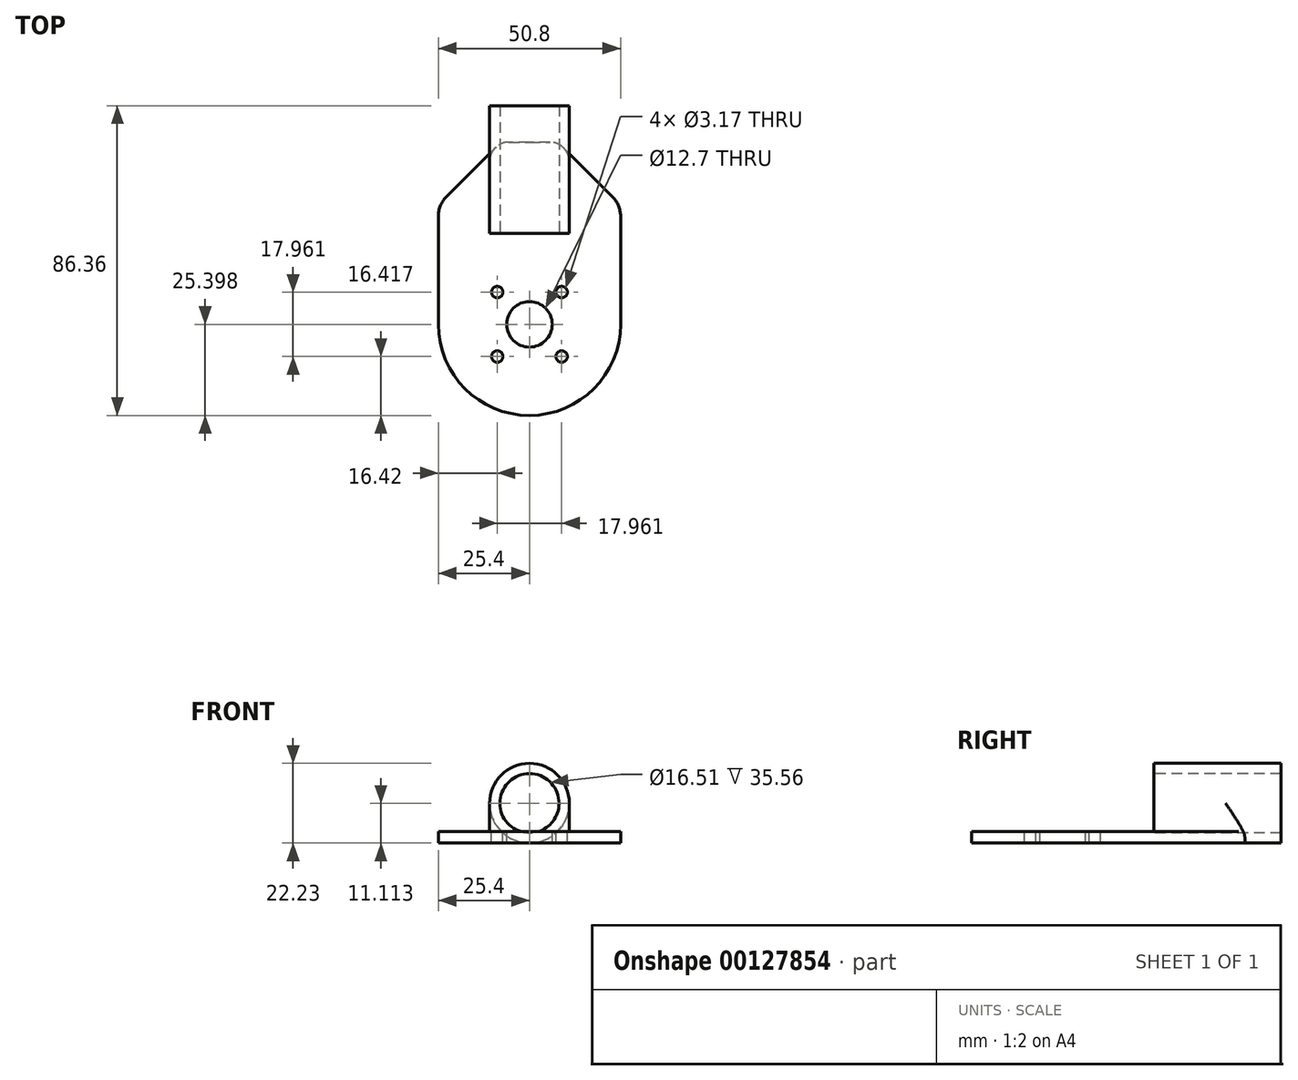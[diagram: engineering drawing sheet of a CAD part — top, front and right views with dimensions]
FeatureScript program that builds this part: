
annotation { "Feature Type Name" : "Feature", "Feature Type Description" : "" }
export const myFeature = defineFeature(function(context is Context, id is Id, definition is map)
    precondition{}
    {
        {
            var Q0;
            Q0=qCreatedBy(makeId("Top.planeOp"),FACE);
            var sketch = newSketch(context, id + "F0", { "sketchPlane" : qUnion([Q0])});
            skCircle(sketch, "E0", {"center": v(0, 0) * mm, "radius": 11.11 * mm});
            skSolve(sketch);
        }
        {
            var Q0;
            Q0 = qSketchRegion(id + "F0", true);
            extrude(context, id + "F1", {"entities" : qUnion([Q0]), "depth" : 10.16 * mm, "hasSecondDirection" : true, "secondDirectionOppositeDirection" : true, "secondDirectionDepth" : 25.4 * mm});
        }
        {
            var Q0;
            Q0=makeQuery(id+"F1.opExtrude","CAP_FACE",FACE,{"disambiguationData":[OSD([sQuery(id+"F0.wireOp",EDGE,"E0")])],"isStart":false});
            var sketch = newSketch(context, id + "F2", { "sketchPlane" : qUnion([Q0])});
            skLineSegment(sketch, "E1.bottom", {"start": v(25.4, -11.11) * mm, "end": v(-25.4, -11.11) * mm});
            skLineSegment(sketch, "E1.top", {"start": v(25.4, -7.94) * mm, "end": v(-25.4, -7.94) * mm});
            skLineSegment(sketch, "E1.left", {"start": v(25.4, -11.11) * mm, "end": v(25.4, -7.94) * mm});
            skLineSegment(sketch, "E1.right", {"start": v(-25.4, -11.11) * mm, "end": v(-25.4, -7.94) * mm});
            skPoint(sketch, "E1.middle", {"position": v(0, -9.53) * mm});
            skSolve(sketch);
        }
        {
            var Q0;
            Q0 = qSketchRegion(id + "F2", true);
            extrude(context, id + "F3", {"entities" : qUnion([Q0]), "operationType" : NewBodyOperationType.ADD, "depth" : 50.8 * mm, "hasSecondDirection" : true, "secondDirectionOppositeDirection" : true, "secondDirectionDepth" : 25.4 * mm});
        }
        {
            var Q0;
            Q0=makeQuery(id+"F3.opExtrude","SWEPT_FACE",FACE,{"disambiguationData":[OSD([sQuery(id+"F2.wireOp",EDGE,"E1.top")])]});
            var sketch = newSketch(context, id + "F4", { "sketchPlane" : qUnion([Q0])});
            skPoint(sketch, "E2", {"position": v(0, 35.56) * mm});
            skCircle(sketch, "E3", {"center": v(-8.98, 26.58) * mm, "radius": 1.59 * mm});
            skCircle(sketch, "E4", {"center": v(-8.98, 44.54) * mm, "radius": 1.59 * mm});
            skCircle(sketch, "E5", {"center": v(8.98, 26.58) * mm, "radius": 1.59 * mm});
            skCircle(sketch, "E6", {"center": v(8.98, 44.54) * mm, "radius": 1.59 * mm});
            skSolve(sketch);
        }
        {
            var Q0;
            Q0 = qSketchRegion(id + "F4", true);
            extrude(context, id + "F5", {"entities" : qUnion([Q0]), "operationType" : NewBodyOperationType.REMOVE, "oppositeDirection" : true, "depth" : 25.4 * mm});
        }
        {
            var Q0;
            Q0=makeQuery(id+"F3.opExtrude","SWEPT_FACE",FACE,{"disambiguationData":[OSD([sQuery(id+"F2.wireOp",EDGE,"E1.bottom")])]});
            var sketch = newSketch(context, id + "F6", { "sketchPlane" : qUnion([Q0])});
            skArc(sketch, "E7", {"start": v(25.4, 35.56) * mm, "mid": v(0, 60.96) * mm, "end": v(-25.4, 35.56) * mm});
            skLineSegment(sketch, "E8", {"start": v(-25.4, 35.56) * mm, "end": v(-25.4, 60.96) * mm});
            skLineSegment(sketch, "E9", {"start": v(-25.4, 60.96) * mm, "end": v(25.4, 60.96) * mm});
            skLineSegment(sketch, "E10", {"start": v(25.4, 60.96) * mm, "end": v(25.4, 35.56) * mm});
            skSolve(sketch);
        }
        {
            var Q0;
            Q0 = qSketchRegion(id + "F6", true);
            extrude(context, id + "F7", {"entities" : qUnion([Q0]), "operationType" : NewBodyOperationType.REMOVE, "oppositeDirection" : true, "depth" : 25.4 * mm});
        }
        {
            var Q0;
            Q0=qCreatedBy(makeId("Top.planeOp"),FACE);
            cPlane(context, id + "F8", {"entities" : qUnion([Q0]), "cplaneType" : CPlaneType.OFFSET, "offset" : 10.16 * mm, "width" : 152.4 * mm, "height" : 152.4 * mm});
        }
        {
            var Q0;
            Q0=qCreatedBy(id+"F8.planeOp",FACE);
            var sketch = newSketch(context, id + "F9", { "sketchPlane" : qUnion([Q0])});
            skArc(sketch, "E11", {"start": v(11.11, 0) * mm, "mid": v(0, 11.11) * mm, "end": v(-11.11, 0) * mm});
            skLineSegment(sketch, "E12", {"start": v(-11.11, 0) * mm, "end": v(-11.11, -8.9) * mm});
            skLineSegment(sketch, "E13", {"start": v(11.11, 0) * mm, "end": v(11.11, -8.9) * mm});
            skLineSegment(sketch, "E14", {"start": v(-11.11, -8.9) * mm, "end": v(11.11, -8.9) * mm});
            skSolve(sketch);
        }
        {
            var Q0;
            Q0 = qSketchRegion(id + "F9", true);
            extrude(context, id + "F10", {"entities" : qUnion([Q0]), "operationType" : NewBodyOperationType.ADD, "oppositeDirection" : true, "depth" : 25.4 * mm});
        }
        {
            var Q0;
            Q0=makeQuery(id+"F3.opExtrude","CAP_EDGE",EDGE,{"disambiguationData":[OSD([sQuery(id+"F2.wireOp",EDGE,"E1.left")])],"isStart":true});
            var Q1;
            Q1=makeQuery(id+"F3.opExtrude","CAP_EDGE",EDGE,{"disambiguationData":[OSD([sQuery(id+"F2.wireOp",EDGE,"E1.right")])],"isStart":true});
            chamfer(context, id + "F11", {"entities" : qUnion([Q0, Q1]), "width" : 17.53 * mm, "tangentPropagation" : true});
        }
        {
            var Q0;
            {var subQ0=sQuery(id+"F2.wireOp",EDGE,"E1.left");Q0=makeQuery(id+"F11.opChamfer","BLEND_EDGE",EDGE,{"blendedFrom":[makeQuery(id+"F3.opExtrude","CAP_EDGE",EDGE,{"disambiguationData":[OSD([subQ0])],"isStart":true}),makeQuery(id+"F3.opExtrude","SWEPT_FACE",FACE,{"disambiguationData":[OSD([subQ0])]})],"blendedInto":[makeQuery(id+"F3.opExtrude","SWEPT_FACE",FACE,{"disambiguationData":[OSD([subQ0])]})]});}
            var Q1;
            {var subQ0=sQuery(id+"F2.wireOp",EDGE,"E1.right");Q1=makeQuery(id+"F11.opChamfer","BLEND_EDGE",EDGE,{"blendedFrom":[makeQuery(id+"F3.opExtrude","CAP_EDGE",EDGE,{"disambiguationData":[OSD([subQ0])],"isStart":true}),makeQuery(id+"F3.opExtrude","SWEPT_FACE",FACE,{"disambiguationData":[OSD([subQ0])]})],"blendedInto":[makeQuery(id+"F3.opExtrude","SWEPT_FACE",FACE,{"disambiguationData":[OSD([subQ0])]})]});}
            fillet(context, id + "F12", {"entities" : qUnion([Q0, Q1]), "radius" : 7.62 * mm, "tangentPropagation" : true, "allowEdgeOverflow" : false});
        }
        {
            var Q0;
            {var subQ0=sQuery(id+"F2.wireOp",EDGE,"E1.top");var subQ1=sQuery(id+"F2.wireOp",EDGE,"E1.left");var subQ2=sQuery(id+"F2.wireOp",EDGE,"E1.bottom");var subQ3=makeQuery(id+"F3.opExtrude","CAP_FACE",FACE,{"disambiguationData":[OSD([subQ2,subQ0,subQ1,sQuery(id+"F2.wireOp",EDGE,"E1.right")])],"isStart":true});Q0=makeQuery(id+"F11.opChamfer","BLEND_EDGE",EDGE,{"blendedFrom":[makeQuery(id+"F3.opExtrude","CAP_EDGE",EDGE,{"disambiguationData":[OSD([subQ1])],"isStart":true}),makeQuery(id+"F3.boolean.opBoolean","SPLIT",FACE,{"disambiguationData":[TD([makeQuery(id+"F3.opExtrude","SWEPT_FACE",FACE,{"disambiguationData":[OSD([subQ1])]})])],"derivedFrom":subQ3})],"blendedInto":[makeQuery(id+"F3.boolean.opBoolean","SPLIT",FACE,{"disambiguationData":[TD([makeQuery(id+"F3.opExtrude","SWEPT_FACE",FACE,{"disambiguationData":[OSD([subQ1])]})])],"derivedFrom":subQ3})]});}
            var Q1;
            {var subQ0=sQuery(id+"F2.wireOp",EDGE,"E1.top");var subQ1=sQuery(id+"F2.wireOp",EDGE,"E1.right");var subQ2=sQuery(id+"F2.wireOp",EDGE,"E1.bottom");var subQ3=makeQuery(id+"F3.opExtrude","CAP_FACE",FACE,{"disambiguationData":[OSD([subQ2,subQ0,sQuery(id+"F2.wireOp",EDGE,"E1.left"),subQ1])],"isStart":true});Q1=makeQuery(id+"F11.opChamfer","BLEND_EDGE",EDGE,{"blendedFrom":[makeQuery(id+"F3.opExtrude","CAP_EDGE",EDGE,{"disambiguationData":[OSD([subQ1])],"isStart":true}),makeQuery(id+"F3.boolean.opBoolean","SPLIT",FACE,{"disambiguationData":[TD([makeQuery(id+"F3.opExtrude","SWEPT_FACE",FACE,{"disambiguationData":[OSD([subQ1])]})])],"derivedFrom":subQ3})],"blendedInto":[makeQuery(id+"F3.boolean.opBoolean","SPLIT",FACE,{"disambiguationData":[TD([makeQuery(id+"F3.opExtrude","SWEPT_FACE",FACE,{"disambiguationData":[OSD([subQ1])]})])],"derivedFrom":subQ3})]});}
            fillet(context, id + "F13", {"entities" : qUnion([Q0, Q1]), "radius" : 5.08 * mm, "tangentPropagation" : true, "allowEdgeOverflow" : false});
        }
        {
            var Q0;
            Q0=makeQuery(id+"F1.opExtrude","CAP_FACE",FACE,{"disambiguationData":[OSD([sQuery(id+"F0.wireOp",EDGE,"E0")])],"isStart":false});
            var sketch = newSketch(context, id + "F14", { "sketchPlane" : qUnion([Q0])});
            skCircle(sketch, "E15", {"center": v(0, 0) * mm, "radius": 8.26 * mm});
            skSolve(sketch);
        }
        {
            var Q0;
            Q0 = qSketchRegion(id + "F14", true);
            extrude(context, id + "F15", {"entities" : qUnion([Q0]), "operationType" : NewBodyOperationType.REMOVE, "endBound" : BoundingType.THROUGH_ALL, "oppositeDirection" : true, "depth" : 25.4 * mm});
        }
        {
            var Q0;
            Q0=makeQuery(id+"F11.opChamfer","BLEND_EDGE",EDGE,{"blendedFrom":[makeQuery(id+"F3.opExtrude","CAP_EDGE",EDGE,{"disambiguationData":[OSD([sQuery(id+"F2.wireOp",EDGE,"E1.right")])],"isStart":true}),makeQuery(id+"F10.opExtrude","SWEPT_FACE",FACE,{"disambiguationData":[OSD([sQuery(id+"F9.wireOp",EDGE,"E12")])]})],"blendedInto":[makeQuery(id+"F10.opExtrude","SWEPT_FACE",FACE,{"disambiguationData":[OSD([sQuery(id+"F9.wireOp",EDGE,"E12")])]})]});
            var Q1;
            Q1=makeQuery(id+"F11.opChamfer","BLEND_EDGE",EDGE,{"blendedFrom":[makeQuery(id+"F3.opExtrude","CAP_EDGE",EDGE,{"disambiguationData":[OSD([sQuery(id+"F2.wireOp",EDGE,"E1.left")])],"isStart":true}),makeQuery(id+"F10.opExtrude","SWEPT_FACE",FACE,{"disambiguationData":[OSD([sQuery(id+"F9.wireOp",EDGE,"E13")])]})],"blendedInto":[makeQuery(id+"F10.opExtrude","SWEPT_FACE",FACE,{"disambiguationData":[OSD([sQuery(id+"F9.wireOp",EDGE,"E13")])]})]});
            fillet(context, id + "F16", {"entities" : qUnion([Q0, Q1]), "radius" : 5.08 * mm, "tangentPropagation" : true, "allowEdgeOverflow" : false});
        }
        {
            var Q0;
            Q0=makeQuery(id+"F1.opExtrude","SWEPT_BODY",BODY,{"disambiguationData":[OSD([sQuery(id+"F0.wireOp",EDGE,"E0")])]});
            var Q1;
            {var subQ0=sQuery(id+"F2.wireOp",EDGE,"E1.bottom");var subQ1=sQuery(id+"F2.wireOp",EDGE,"E1.right");Q1=makeQuery(id+"F3.boolean.opBoolean","SPLIT",EDGE,{"disambiguationData":[TD([makeQuery(id+"F3.opExtrude","SWEPT_FACE",FACE,{"disambiguationData":[OSD([subQ1])]})])],"derivedFrom":makeQuery(id+"F3.opExtrude","CAP_EDGE",EDGE,{"disambiguationData":[OSD([subQ0])],"isStart":true})});}
            transform(context, id + "F17", {"entities" : qUnion([Q0]), "transformType" : TransformType.ROTATION, "transformAxis" : qUnion([Q1]), "angle" : 270 * degree, "makeCopy" : false});
        }
        {
            var Q0;
            Q0=makeQuery(id+"F3.opExtrude","SWEPT_FACE",FACE,{"disambiguationData":[OSD([sQuery(id+"F2.wireOp",EDGE,"E1.top")])]});
            var sketch = newSketch(context, id + "F18", { "sketchPlane" : qUnion([Q0])});
            skPoint(sketch, "E16", {"position": v(0, -61.91) * mm});
            skPoint(sketch, "E17.orphan", {"position": v(-8.98, -52.93) * mm});
            skPoint(sketch, "E18.orphan", {"position": v(8.98, -52.93) * mm});
            skPoint(sketch, "E19.end.orphan", {"position": v(8.98, -70.9) * mm});
            skPoint(sketch, "E20.start.orphan", {"position": v(-8.98, -70.9) * mm});
            skCircle(sketch, "E21", {"center": v(0, -61.91) * mm, "radius": 6.35 * mm});
            skSolve(sketch);
        }
        {
            var Q0;
            Q0 = qSketchRegion(id + "F18", true);
            extrude(context, id + "F19", {"entities" : qUnion([Q0]), "operationType" : NewBodyOperationType.REMOVE, "endBound" : BoundingType.THROUGH_ALL, "oppositeDirection" : true, "depth" : 25.4 * mm});
        }
    });
